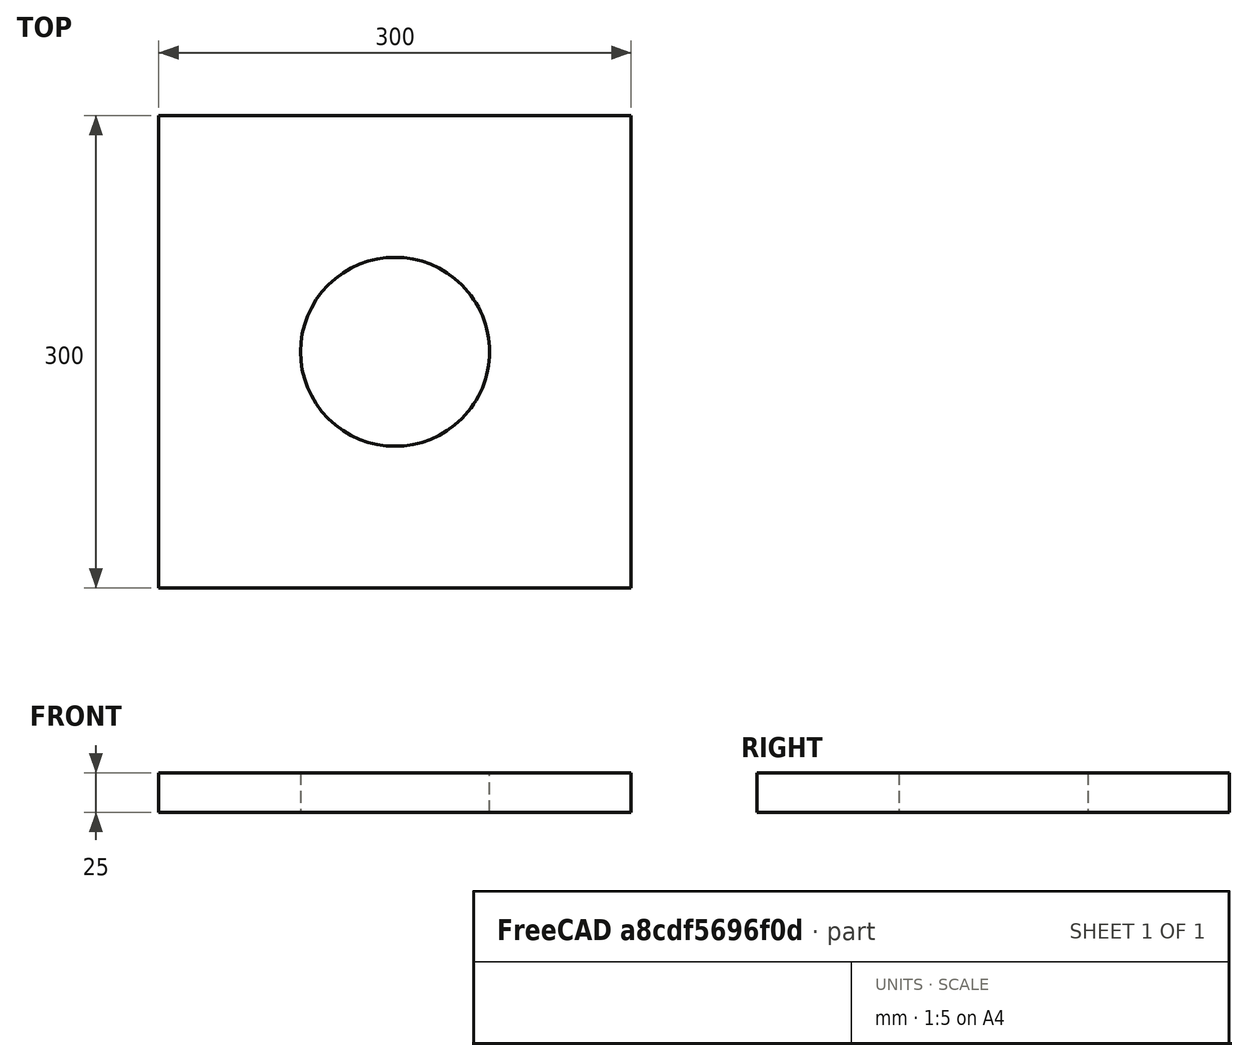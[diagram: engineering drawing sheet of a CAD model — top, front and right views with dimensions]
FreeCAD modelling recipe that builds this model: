
FCSTD DOCUMENT  (FreeCAD 0.21R33694 (Git))
Label: Lug_Displacement_Example
License: All rights reserved
LicenseURL: http://en.wikipedia.org/wiki/All_rights_reserved
objects: Part::FeaturePython×5, Sketcher::SketchObject×2, Part::Extrusion×2, Fem::FemSolverObjectPython×1, Fem::ConstraintFixed×1, Fem::ConstraintPressure×1, Part::MultiFuse×1, App::MaterialObjectPython×1, Fem::FemMeshObjectPython×1, Fem::ConstraintDisplacement×1, Fem::FemAnalysis×1
note: 10 computed .brp shape members not serialized (recipe doc carries the construction recipe); baked Part::Feature solids carry a one-line shape summary decoded from their .brp

FEATURE [Sketcher::SketchObject] Sketch
  FullyConstrained = true
  Placement = pos=(150,0,0) rot=(0,0,1;0rad)
  sketch-geometry (5):
    g0: LineSegment StartX=0 StartY=0 StartZ=0 EndX=300 EndY=0 EndZ=0
    g1: LineSegment StartX=300 StartY=0 StartZ=0 EndX=300 EndY=300 EndZ=0
    g2: LineSegment StartX=300 StartY=300 StartZ=0 EndX=0 EndY=300 EndZ=0
    g3: LineSegment StartX=0 StartY=300 StartZ=0 EndX=0 EndY=0 EndZ=0
    g4: Circle CenterX=150 CenterY=150 CenterZ=0 NormalX=0 NormalY=0 NormalZ=1 AngleXU=0 Radius=60
  constraints (14):
    c: Coincident(g0,g1)
    c: Coincident(g1,g2)
    c: Coincident(g2,g3)
    c: Coincident(g3,g0)
    c: Horizontal(g0)
    c: Horizontal(g2)
    c: Vertical(g1)
    c: Vertical(g3)
    c: Coincident(g0,g-1)
    c: DistanceY(g1,g1) = 300
    c: DistanceX(g0,g0) = 300
    c: DistanceX(g0,g4) = 150
    c: DistanceY(g0,g4) = 150
    c: Radius(g4) = 60
FEATURE [Part::Extrusion] Extrude
  Base = -> Sketch
  Dir = (0,0,1)
  DirMode = 2
  FaceMakerClass = Part::FaceMakerBullseye
  LengthFwd = 25
  LengthRev = 0
  Solid = true
  Symmetric = false
FEATURE [Fem::FemSolverObjectPython] SolverCcxTools  # FEM object (typed FeaturePython)
  AnalysisType = 0
  BeamShellResultOutput3D = false
  BucklingFactors = 1
  EigenmodeHighLimit = 1000000
  EigenmodeLowLimit = 0
  EigenmodesCount = 10
  GeometricalNonlinearity = 0
  IterationsControlParameterCutb = 0.25,0.5,0.75,0.85,,,1.5,
  IterationsControlParameterIter = 4,8,9,200,10,400,,200,,
  IterationsControlParameterTimeUse = false
  IterationsThermoMechMaximum = 200
  IterationsUserDefinedIncrementations = false
  IterationsUserDefinedTimeStepLength = false
  MaterialNonlinearity = 0
  MatrixSolverType = 0
  SplitInputWriter = false
  ThermoMechSteadyState = true
  TimeEnd = 1
  TimeInitialStep = 1
FEATURE [Fem::ConstraintFixed] ConstraintFixed001
  NormalDirection = (0,-1,0)
  Normals = (16) [(0,-1,0),(0,-1,0),(0,-1,0),(0,-1,0),(0,-1,0),(0,-1,0),(0,-1,0),(0,-1,0),(0,-1,0),(0,-1,0),(0,-1,0),(0,-1,0),(0,-1,0),(0,-1,0),(0,-1,0),(0,-1,0)]
  Points = (16) [(150,0,25),(250,0,25),(350,0,25),(450,0,25),(150,0,16.6667),(250,0,16.6667),(350,0,16.6667),(450,0,16.6667),(150,0,8.33333),(250,0,8.33333),+6 more]
  References = -> [Extrude]
  Scale = 13
FEATURE [Fem::ConstraintPressure] ConstraintPressure
  NormalDirection = (1,-1e-16,0)
  Normals = (16) [(-1,0,0),(0.5,-0.866025,0),(0.5,0.866025,0),(-1,2.44929e-16,0),(-1,0,0),(0.5,-0.866025,0),(0.5,0.866025,0),(-1,2.44929e-16,0),(-1,0,0),+7 more]
  Points = (16) [(360,150,25),(270,201.962,25),(270,98.0385,25),(360,150,25),(360,150,16.6667),(270,201.962,16.6667),(270,98.0385,16.6667),(360,150,16.6667),+8 more]
  Pressure = 100
  References = -> [Extrude]
  Scale = 15
FEATURE [Sketcher::SketchObject] Sketch001
  FullyConstrained = true
  sketch-geometry (2):
    g0: LineSegment StartX=150 StartY=300 StartZ=0 EndX=450 EndY=0 EndZ=0
    g1: LineSegment StartX=150 StartY=0 StartZ=0 EndX=450 EndY=300 EndZ=0
  constraints (8):
    c: DistanceX(g1) = 150
    c: DistanceY(g1,g-1) = 0
    c: DistanceY(g0,g-1) = 0
    c: DistanceX(g1,g0) = 300
    c: DistanceX(g-1,g0) = 150
    c: DistanceX(g-1,g1) = 450
    c: DistanceY(g-1,g0) = 300
    c: DistanceY(g-1,g1) = 300
FEATURE [Part::Extrusion] Extrude001
  Base = -> Sketch001
  Dir = (0,0,1)
  DirMode = 0
  FaceMakerClass = Part::FaceMakerBullseye
  LengthFwd = 25
  LengthRev = 0
  Solid = false
  Symmetric = false
FEATURE [Part::FeaturePython] Slice  # WARN: FeaturePython — macro-defined, semantics opaque (R4)
  Base = -> Extrude
  Mode = 1
  Tolerance = 0
  Tools = -> [Extrude001]
FEATURE [Part::FeaturePython] Slice_child0  label="Slice.0"  # WARN: FeaturePython — macro-defined, semantics opaque (R4)
  Base = -> Slice
  FilterType = 1
  Invert = false
  OverrideMaxVal = 0
  WindowFrom = 80
  WindowTo = 100
  items = 0
FEATURE [Part::FeaturePython] Slice_child1  label="Slice.1"  # WARN: FeaturePython — macro-defined, semantics opaque (R4)
  Base = -> Slice
  FilterType = 1
  Invert = false
  OverrideMaxVal = 0
  WindowFrom = 80
  WindowTo = 100
  items = 1
FEATURE [Part::FeaturePython] Slice_child2  label="Slice.2"  # WARN: FeaturePython — macro-defined, semantics opaque (R4)
  Base = -> Slice
  FilterType = 1
  Invert = false
  OverrideMaxVal = 0
  WindowFrom = 80
  WindowTo = 100
  items = 2
FEATURE [Part::FeaturePython] Slice_child3  label="Slice.3"  # WARN: FeaturePython — macro-defined, semantics opaque (R4)
  Base = -> Slice
  FilterType = 1
  Invert = false
  OverrideMaxVal = 0
  WindowFrom = 80
  WindowTo = 100
  items = 3
FEATURE [Part::MultiFuse] Fusion001  label="Fusion_25mm"
  Shapes = -> [Slice_child0,Slice_child1,Slice_child2,Slice_child3]
FEATURE [App::MaterialObjectPython] MaterialSolid  # material (typed FeaturePython)
  Category = 0
  Material = AuthorAndLicense=(c) 2014 M. Münch - GNU Lesser General Public License (LGPL),CardName=Steel-St-E-315,Density=7800 kg/m^3,Father=Metal,+13 more (map truncated)
FEATURE [Fem::FemMeshObjectPython] FEMMeshGmsh  # FEM object (typed FeaturePython)
  Algorithm2D = 0
  Algorithm3D = 0
  CharacteristicLengthMax = 0
  CharacteristicLengthMin = 0
  CoherenceMesh = true
  ElementDimension = 0
  ElementOrder = 1
  GeometryTolerance = 1e-06
  GroupsOfNodes = false
  HighOrderOptimize = 0
  MeshSizeFromCurvature = 12
  OptimizeNetgen = false
  OptimizeStd = true
  Part = -> Fusion001
  RecombinationAlgorithm = 0
  Recombine3DAll = false
  RecombineAll = false
  SecondOrderLinear = false
FEATURE [Fem::ConstraintDisplacement] ConstraintDisplacement
  NormalDirection = (1.04e-14,-1,0)
  Normals = (16) [(-0.707107,-0.707107,0),(-0.258819,-0.965926,0),(0.258819,-0.965926,0),(0.707107,-0.707107,0),(-0.707107,-0.707107,0),(-0.258819,-0.965926,0),+10 more]
  Points = (16) [(342.426,192.426,25),(315.529,207.956,25),(284.471,207.956,25),(257.574,192.426,25),(342.426,192.426,16.6667),(315.529,207.956,16.6667),+10 more]
  References = -> [Fusion001]
  Scale = 7
  hasXFormula = false
  hasYFormula = false
  hasZFormula = false
  rotxFix = false
  rotxFree = true
  rotyFix = false
  rotyFree = true
  rotzFix = false
  rotzFree = true
  useFlowSurfaceForce = false
  xDisplacement = 0
  xFix = false
  xFree = true
  xRotation = 0
  yDisplacement = 1
  yFix = false
  yFree = false
  yRotation = 0
  zDisplacement = 0
  zFix = false
  zFree = true
  zRotation = 0
FEATURE [Fem::FemAnalysis] Analysis
  Group = -> [SolverCcxTools,MaterialSolid,ConstraintFixed001,ConstraintPressure,FEMMeshGmsh,ConstraintDisplacement]
